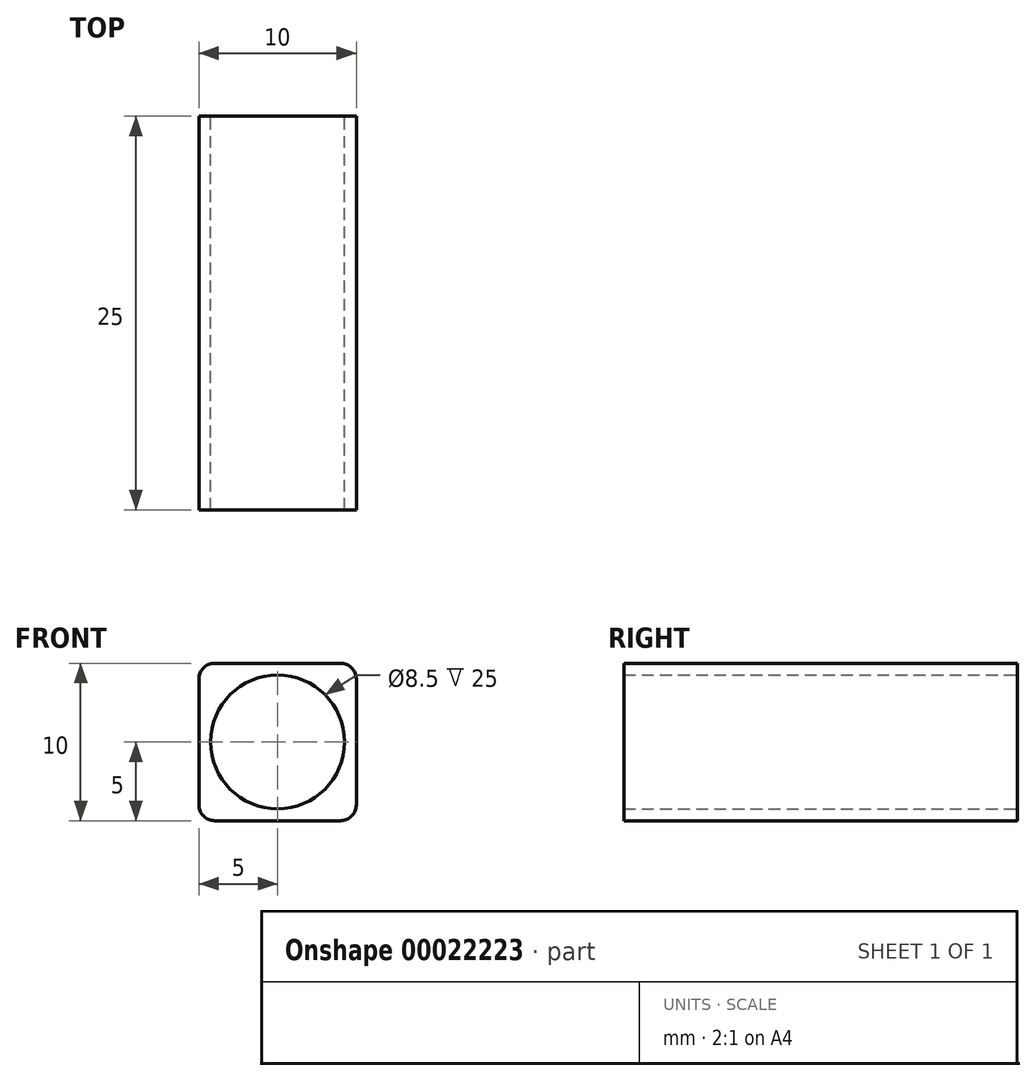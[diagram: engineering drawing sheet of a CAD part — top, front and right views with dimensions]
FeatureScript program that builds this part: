
annotation { "Feature Type Name" : "Feature", "Feature Type Description" : "" }
export const myFeature = defineFeature(function(context is Context, id is Id, definition is map)
    precondition{}
    {
        {
            var Q0;
            Q0=qCreatedBy(makeId("Front.planeOp"),FACE);
            var sketch = newSketch(context, id + "F0", { "sketchPlane" : qUnion([Q0])});
            skLineSegment(sketch, "E0.rect.bottom", {"start": v(-5, -5) * mm, "end": v(5, -5) * mm});
            skLineSegment(sketch, "E0.rect.top", {"start": v(-5, 5) * mm, "end": v(5, 5) * mm});
            skLineSegment(sketch, "E0.rect.left", {"start": v(-5, -5) * mm, "end": v(-5, 5) * mm});
            skLineSegment(sketch, "E0.rect.right", {"start": v(5, -5) * mm, "end": v(5, 5) * mm});
            skPoint(sketch, "E0.rect.middle", {"position": v(0, 0) * mm});
            skCircle(sketch, "E1", {"center": v(0, 0) * mm, "radius": 4.25 * mm});
            skSolve(sketch);
        }
        {
            var Q0;
            Q0=makeQuery(id+"F0.imprint","IMPRINT",FACE,{"disambiguationData":[TD([[makeQuery(id+"F0.imprint","IMPRINT",EDGE,{"derivedFrom":sQuery(id+"F0.wireOp",EDGE,"E0.rect.bottom")}),1.0]])]});
            extrude(context, id + "F1", {"entities" : qUnion([Q0]), "depth" : 25 * mm});
        }
        {
            var Q0;
            Q0=makeQuery(id+"F1.opExtrude","SWEPT_EDGE",EDGE,{"disambiguationData":[OSD([sQuery(id+"F0.wireOp",EDGE,"E0.rect.top"),sQuery(id+"F0.wireOp",EDGE,"E0.rect.left")])]});
            var Q1;
            Q1=makeQuery(id+"F1.opExtrude","SWEPT_EDGE",EDGE,{"disambiguationData":[OSD([sQuery(id+"F0.wireOp",EDGE,"E0.rect.bottom"),sQuery(id+"F0.wireOp",EDGE,"E0.rect.left")])]});
            var Q2;
            Q2=makeQuery(id+"F1.opExtrude","SWEPT_EDGE",EDGE,{"disambiguationData":[OSD([sQuery(id+"F0.wireOp",EDGE,"E0.rect.top"),sQuery(id+"F0.wireOp",EDGE,"E0.rect.right")])]});
            var Q3;
            Q3=makeQuery(id+"F1.opExtrude","SWEPT_EDGE",EDGE,{"disambiguationData":[OSD([sQuery(id+"F0.wireOp",EDGE,"E0.rect.bottom"),sQuery(id+"F0.wireOp",EDGE,"E0.rect.right")])]});
            fillet(context, id + "F2", {"entities" : qUnion([Q0, Q1, Q2, Q3]), "radius" : 1 * mm, "allowEdgeOverflow" : false});
        }
    });
